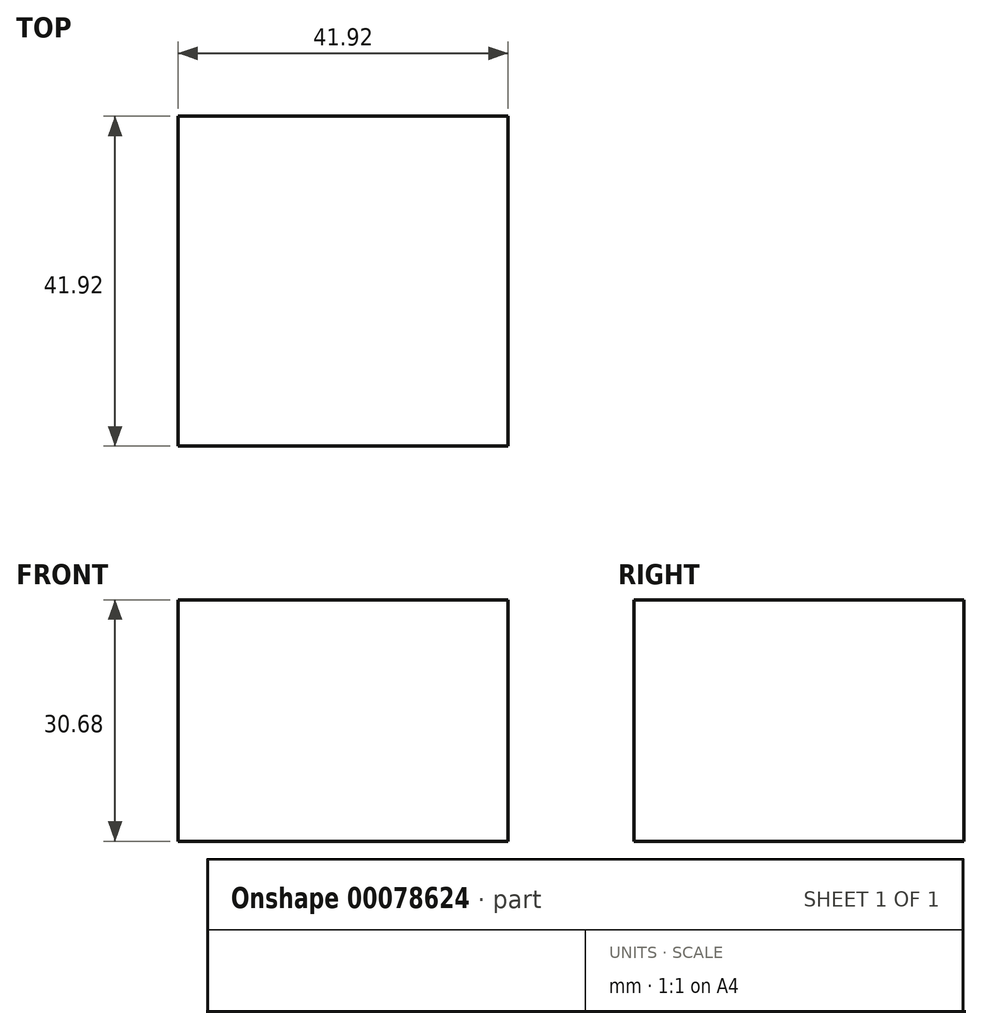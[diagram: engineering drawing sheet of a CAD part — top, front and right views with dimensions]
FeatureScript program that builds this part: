
annotation { "Feature Type Name" : "Feature", "Feature Type Description" : "" }
export const myFeature = defineFeature(function(context is Context, id is Id, definition is map)
    precondition{}
    {
        {
            var Q0;
            Q0=qCreatedBy(makeId("Top.planeOp"),FACE);
            var sketch = newSketch(context, id + "F0", { "sketchPlane" : qUnion([Q0])});
            skLineSegment(sketch, "E0.bottom", {"start": v(0, 0) * mm, "end": v(41.92, 0) * mm});
            skLineSegment(sketch, "E0.top", {"start": v(0, 41.92) * mm, "end": v(41.92, 41.92) * mm});
            skLineSegment(sketch, "E0.left", {"start": v(0, 0) * mm, "end": v(0, 41.92) * mm});
            skLineSegment(sketch, "E0.right", {"start": v(41.92, 0) * mm, "end": v(41.92, 41.92) * mm});
            skLineSegment(sketch, "E1.bottom", {"start": v(38.38, 41.92) * mm, "end": v(41.92, 41.92) * mm});
            skLineSegment(sketch, "E1.top", {"start": v(38.38, 41.92) * mm, "end": v(41.92, 41.92) * mm});
            skLineSegment(sketch, "E1.left", {"start": v(38.38, 41.92) * mm, "end": v(38.38, 41.92) * mm});
            skLineSegment(sketch, "E1.right", {"start": v(41.92, 41.92) * mm, "end": v(41.92, 41.92) * mm});
            skSolve(sketch);
        }
        {
            var Q0;
            Q0=makeQuery(id+"F0.imprint","IMPRINT",FACE,{"disambiguationData":[TD([[makeQuery(id+"F0.imprint","IMPRINT",EDGE,{"derivedFrom":sQuery(id+"F0.wireOp",EDGE,"E0.bottom")}),1.0]])]});
            extrude(context, id + "F1", {"entities" : qUnion([Q0]), "depth" : 10 * mm});
        }
        {
            var Q0;
            Q0=makeQuery(id+"F1.opExtrude","CAP_FACE",FACE,{"disambiguationData":[OSD([sQuery(id+"F0.wireOp",EDGE,"E0.bottom"),sQuery(id+"F0.wireOp",EDGE,"E0.top"),sQuery(id+"F0.wireOp",EDGE,"E0.left"),sQuery(id+"F0.wireOp",EDGE,"E0.right"),sQuery(id+"F0.wireOp",EDGE,"E1.top")])],"isStart":false});
            extrude(context, id + "F2", {"entities" : qUnion([Q0]), "operationType" : NewBodyOperationType.ADD, "depth" : 20.68 * mm});
        }
    });
